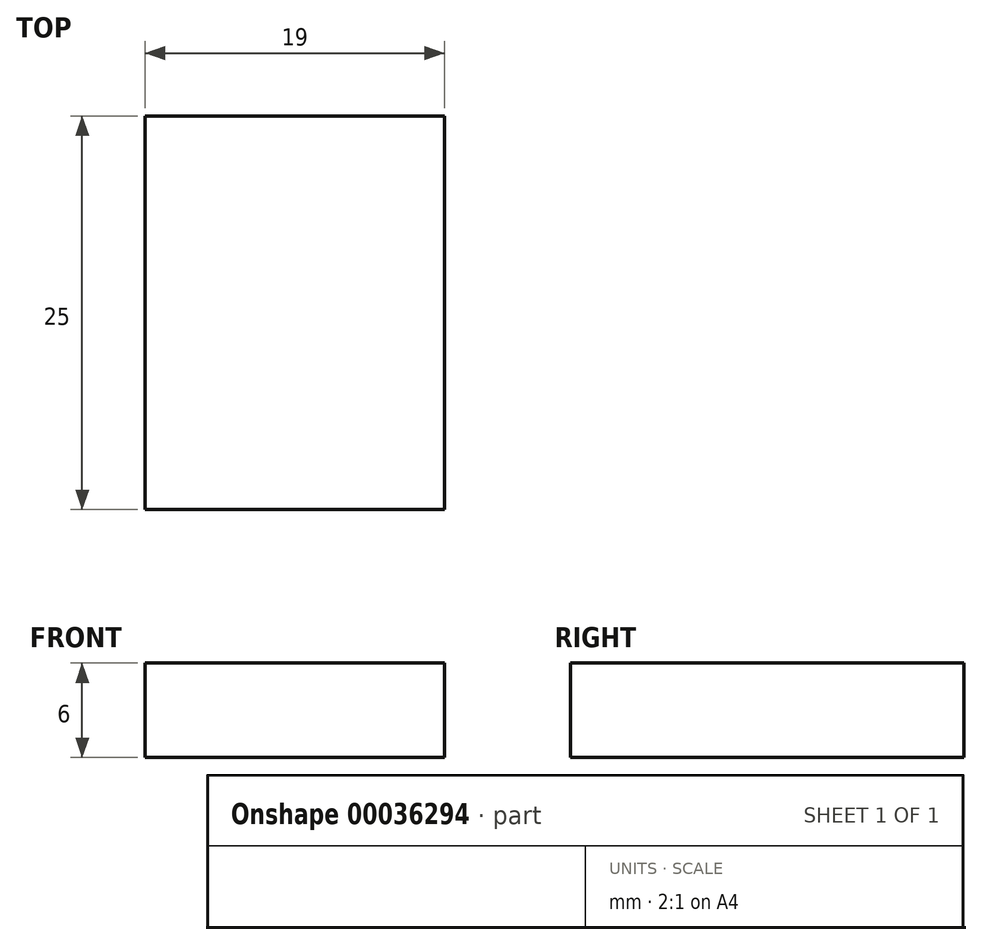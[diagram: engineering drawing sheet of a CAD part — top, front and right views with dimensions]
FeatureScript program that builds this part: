
annotation { "Feature Type Name" : "Feature", "Feature Type Description" : "" }
export const myFeature = defineFeature(function(context is Context, id is Id, definition is map)
    precondition{}
    {
        {
            var Q0;
            Q0=qCreatedBy(makeId("Top.planeOp"),FACE);
            var sketch = newSketch(context, id + "F0", { "sketchPlane" : qUnion([Q0])});
            skLineSegment(sketch, "E0.bottom", {"start": v(0, 0) * mm, "end": v(19, 0) * mm});
            skLineSegment(sketch, "E0.top", {"start": v(0, -25) * mm, "end": v(19, -25) * mm});
            skLineSegment(sketch, "E0.left", {"start": v(0, 0) * mm, "end": v(0, -25) * mm});
            skLineSegment(sketch, "E0.right", {"start": v(19, 0) * mm, "end": v(19, -25) * mm});
            skSolve(sketch);
        }
        {
            var Q0;
            Q0=makeQuery(id+"F0.imprint","IMPRINT",FACE,{"disambiguationData":[TD([[makeQuery(id+"F0.imprint","IMPRINT",EDGE,{"derivedFrom":sQuery(id+"F0.wireOp",EDGE,"E0.bottom")}),-1.0]])]});
            extrude(context, id + "F1", {"entities" : qUnion([Q0]), "depth" : 6 * mm});
        }
    });
